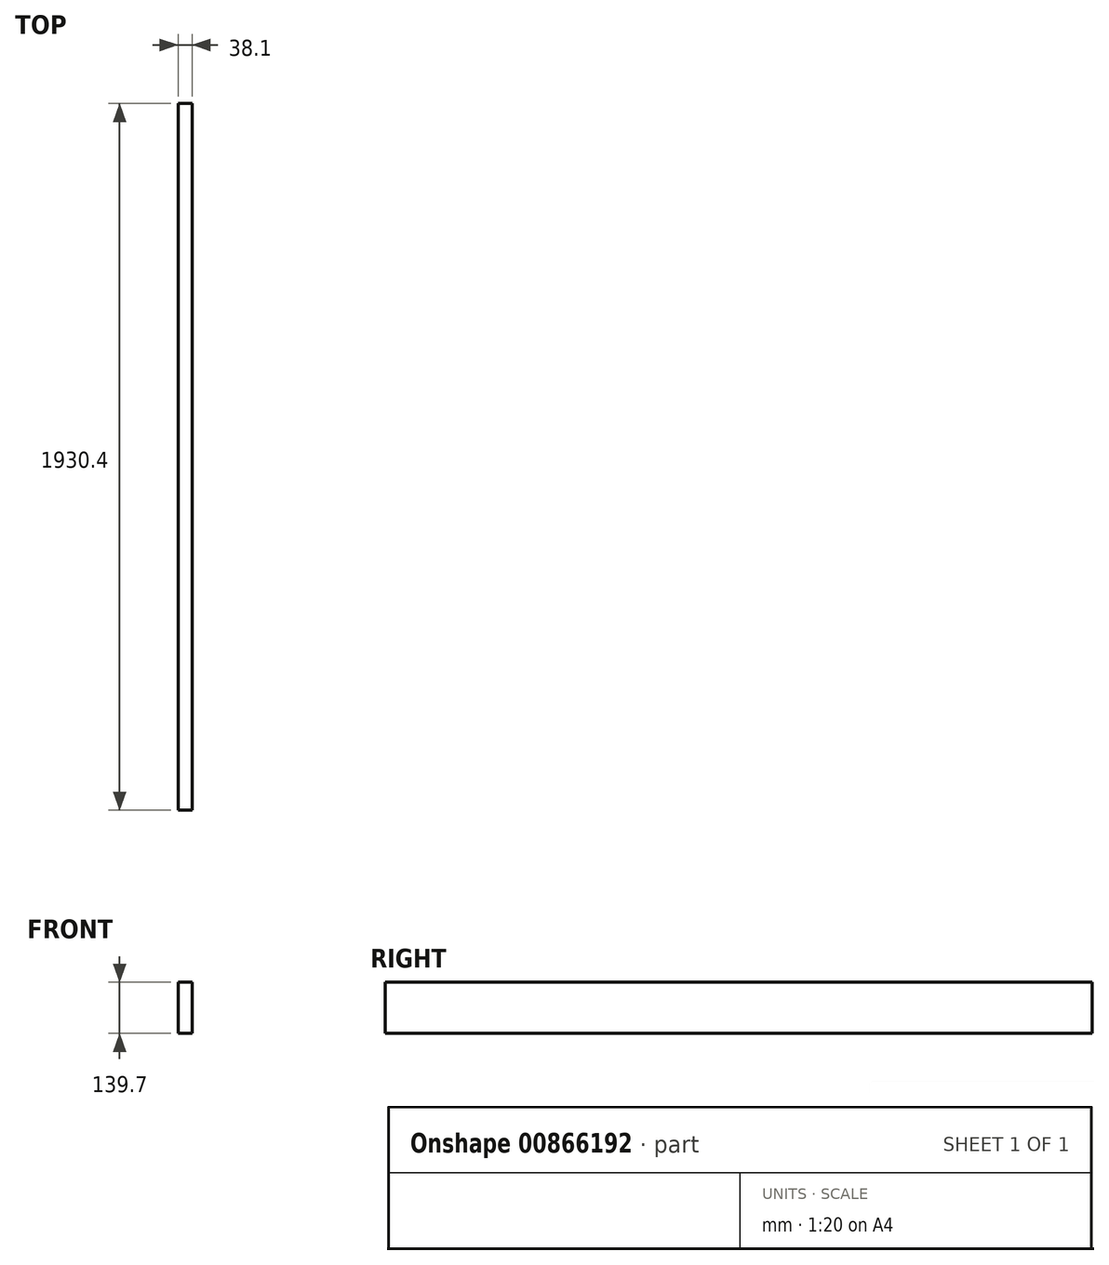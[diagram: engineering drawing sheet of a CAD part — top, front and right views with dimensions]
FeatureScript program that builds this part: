
annotation { "Feature Type Name" : "Feature", "Feature Type Description" : "" }
export const myFeature = defineFeature(function(context is Context, id is Id, definition is map)
    precondition{}
    {
        {
            var Q0;
            Q0=qCreatedBy(makeId("Front.planeOp"),FACE);
            var sketch = newSketch(context, id + "F0", { "sketchPlane" : qUnion([Q0])});
            skLineSegment(sketch, "E0.bottom", {"start": v(-128.66, 126.9) * mm, "end": v(-90.56, 126.9) * mm});
            skLineSegment(sketch, "E0.top", {"start": v(-128.66, -12.8) * mm, "end": v(-90.56, -12.8) * mm});
            skLineSegment(sketch, "E0.left", {"start": v(-128.66, 126.9) * mm, "end": v(-128.66, -12.8) * mm});
            skLineSegment(sketch, "E0.right", {"start": v(-90.56, 126.9) * mm, "end": v(-90.56, -12.8) * mm});
            skSolve(sketch);
        }
        {
            var Q0;
            Q0 = qSketchRegion(id + "F0", true);
            extrude(context, id + "F1", {"entities" : qUnion([Q0]), "oppositeDirection" : true, "depth" : 1930.4 * mm, "offsetDistance" : 25.4 * mm});
        }
    });
